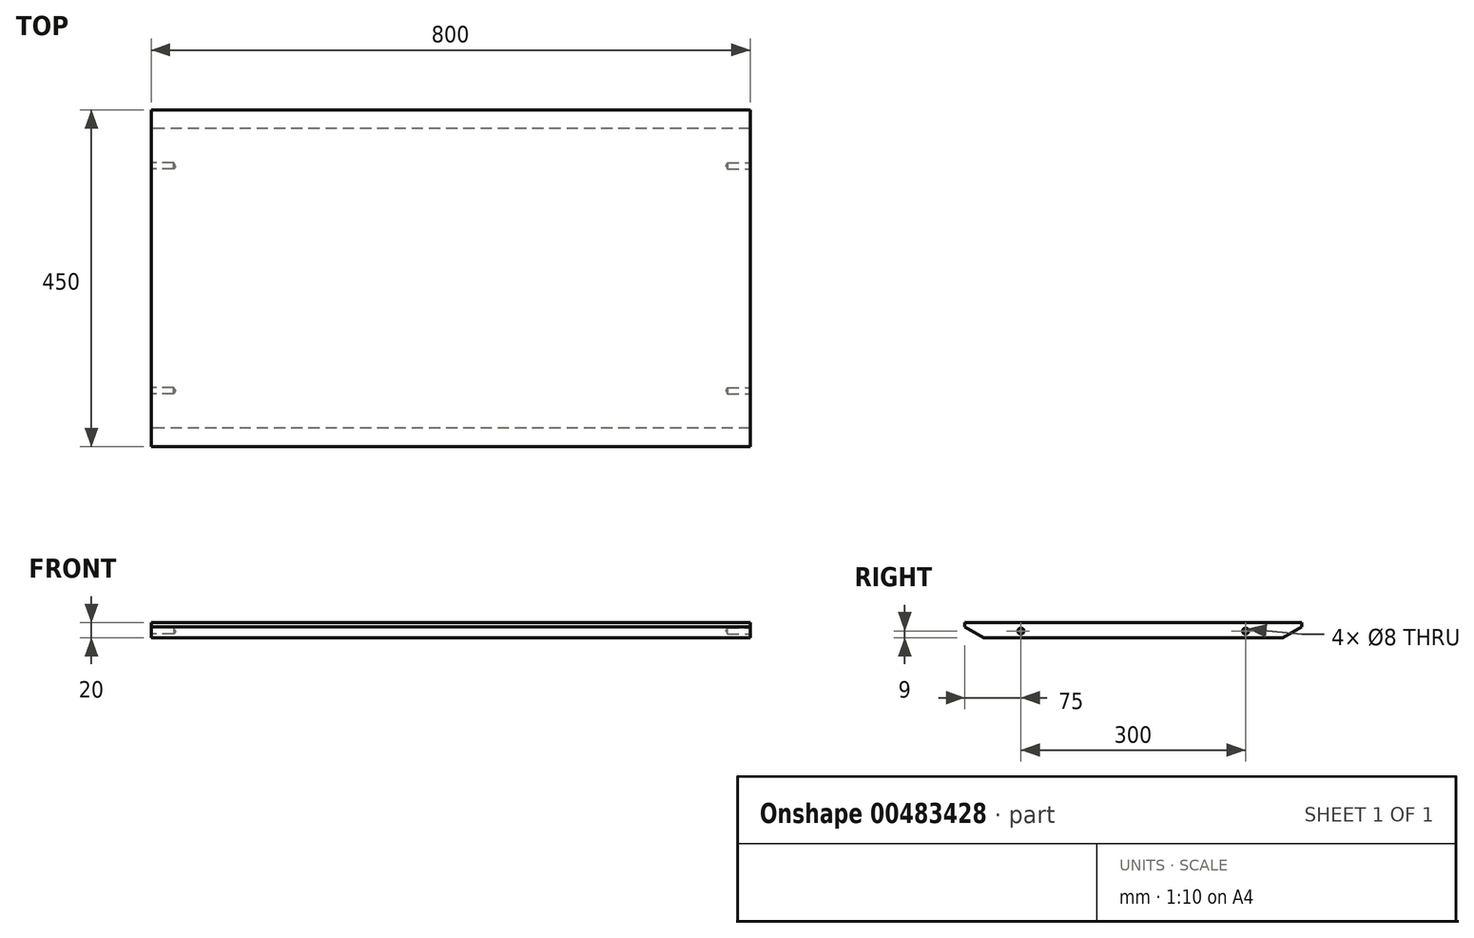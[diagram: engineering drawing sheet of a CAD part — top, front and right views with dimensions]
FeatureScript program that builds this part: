
annotation { "Feature Type Name" : "Feature", "Feature Type Description" : "" }
export const myFeature = defineFeature(function(context is Context, id is Id, definition is map)
    precondition{}
    {
        {
            var Q0;
            Q0=qCreatedBy(makeId("Top.planeOp"),FACE);
            var sketch = newSketch(context, id + "F0", { "sketchPlane" : qUnion([Q0])});
            skLineSegment(sketch, "E0.bottom", {"start": v(400, -225) * mm, "end": v(-400, -225) * mm});
            skLineSegment(sketch, "E0.top", {"start": v(400, 225) * mm, "end": v(-400, 225) * mm});
            skLineSegment(sketch, "E0.left", {"start": v(400, -225) * mm, "end": v(400, 225) * mm});
            skLineSegment(sketch, "E0.right", {"start": v(-400, -225) * mm, "end": v(-400, 225) * mm});
            skPoint(sketch, "E0.middle", {"position": v(0, 0) * mm});
            skSolve(sketch);
        }
        {
            var Q0;
            Q0=qSketchRegion(id+"F0",true);
            extrude(context, id + "F1", {"entities" : qUnion([Q0]), "depth" : 20 * mm});
        }
        {
            var Q0;
            Q0=qCreatedBy(makeId("Right.planeOp"),FACE);
            var sketch = newSketch(context, id + "F2", { "sketchPlane" : qUnion([Q0])});
            skLineSegment(sketch, "E1", {"start": v(200, 0) * mm, "end": v(-200, 0) * mm});
            skLineSegment(sketch, "E2", {"start": v(-200, 0) * mm, "end": v(-234.64, 20) * mm});
            skLineSegment(sketch, "E3", {"start": v(-234.64, 20) * mm, "end": v(234.64, 20) * mm});
            skLineSegment(sketch, "E4", {"start": v(234.64, 20) * mm, "end": v(200, 0) * mm});
            skSolve(sketch);
        }
        {
            var Q0;
            Q0=qSketchRegion(id+"F2",true);
            extrude(context, id + "F3", {"entities" : qUnion([Q0]), "operationType" : NewBodyOperationType.INTERSECT, "endBound" : BoundingType.THROUGH_ALL, "depth" : 25 * mm, "hasSecondDirection" : true, "secondDirectionBound" : SecondDirectionBoundingType.THROUGH_ALL, "secondDirectionOppositeDirection" : true, "secondDirectionDepth" : 25 * mm});
        }
        {
            var Q0;
            Q0=makeQuery(id+"F1.opExtrude","SWEPT_FACE",FACE,{"disambiguationData":[OSD([sQuery(id+"F0.wireOp",EDGE,"E0.right")])]});
            var sketch = newSketch(context, id + "F4", { "sketchPlane" : qUnion([Q0])});
            skPoint(sketch, "E5", {"position": v(-150, 9) * mm});
            skPoint(sketch, "E6", {"position": v(150, 9) * mm});
            skSolve(sketch);
        }
        {
            var Q0;
            Q0=makeQuery(id+"F1.opExtrude","SWEPT_FACE",FACE,{"disambiguationData":[OSD([sQuery(id+"F0.wireOp",EDGE,"E0.left")])]});
            var sketch = newSketch(context, id + "F5", { "sketchPlane" : qUnion([Q0])});
            skPoint(sketch, "E7", {"position": v(-150, 9) * mm});
            skPoint(sketch, "E8", {"position": v(150, 9) * mm});
            skSolve(sketch);
        }
        {
            var Q0;
            Q0=sQuery(id+"F4.wireOp",VERTEX,"E5");
            var Q1;
            Q1=sQuery(id+"F4.wireOp",VERTEX,"E6");
            var Q2;
            Q2=sQuery(id+"F5.wireOp",VERTEX,"E8");
            var Q3;
            Q3=sQuery(id+"F5.wireOp",VERTEX,"E7");
            var Q4;
            Q4=makeQuery(id+"F1.opExtrude","SWEPT_BODY",BODY,{"disambiguationData":[OSD([sQuery(id+"F0.wireOp",EDGE,"E0.bottom"),sQuery(id+"F0.wireOp",EDGE,"E0.top"),sQuery(id+"F0.wireOp",EDGE,"E0.left"),sQuery(id+"F0.wireOp",EDGE,"E0.right")])]});
            hole(context, id + "F6", {"style" : HoleStyle.SIMPLE, "endStyle" : HoleEndStyle.BLIND, "standardTappedOrClearance" : lookupTablePath({ "standard" : "ISO", "size" : "8", "type" : "Drilled" }), "standardBlindInLast" : lookupTablePath({ "standard" : "ISO", "size" : "8", "type" : "Drilled" }), "holeDiameter" : 8 * mm, "holeDepth" : 30 * mm, "isTappedThrough" : true, "tappedDepth" : 12 * mm, "tapClearance" : 3, "locations" : qUnion([Q0, Q1, Q2, Q3]), "scope" : qUnion([Q4])});
        }
    });
